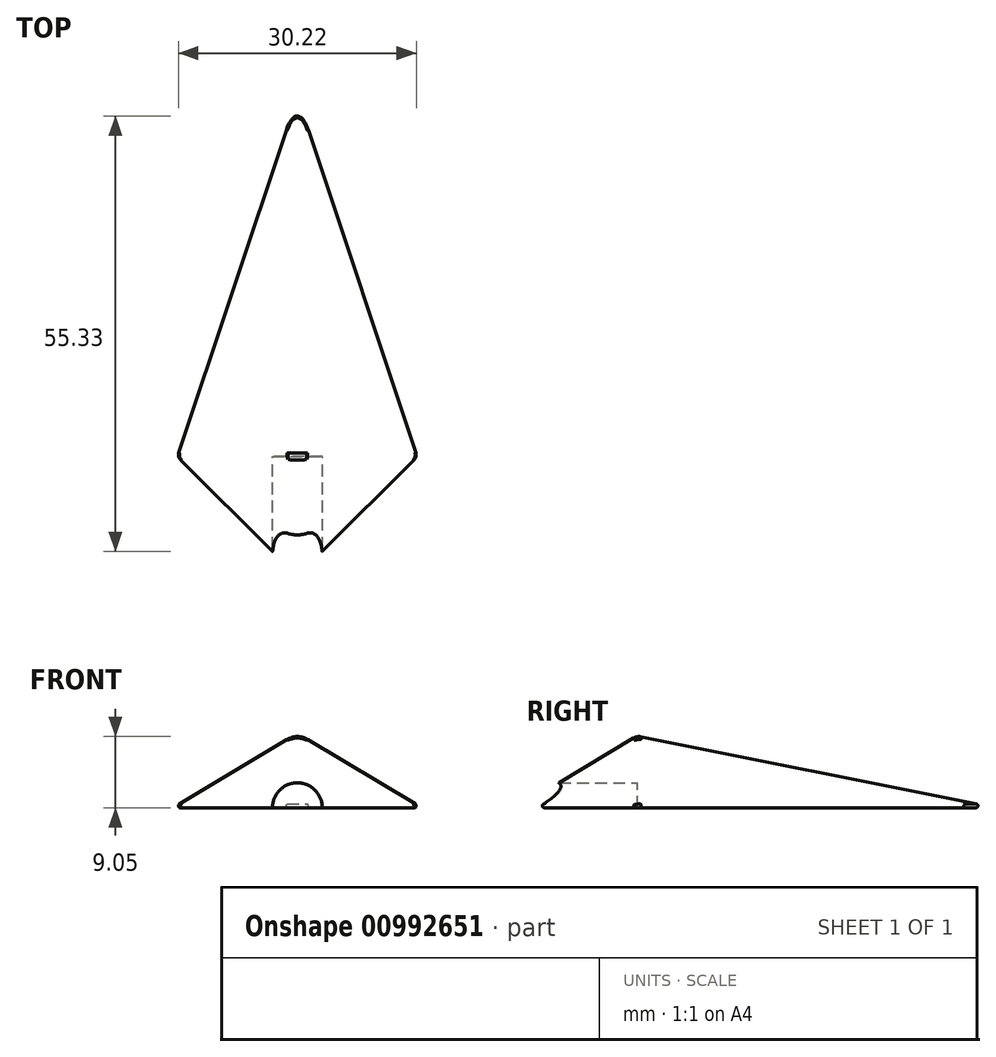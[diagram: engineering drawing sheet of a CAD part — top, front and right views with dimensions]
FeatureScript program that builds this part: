
annotation { "Feature Type Name" : "Feature", "Feature Type Description" : "" }
export const myFeature = defineFeature(function(context is Context, id is Id, definition is map)
    precondition{}
    {
        {
            var Q0;
            Q0=qCreatedBy(makeId("Top.planeOp"),FACE);
            var sketch = newSketch(context, id + "F0", { "sketchPlane" : qUnion([Q0])});
            skLineSegment(sketch, "E0", {"start": v(-15.88, 0) * mm, "end": v(15.88, 0) * mm});
            skLineSegment(sketch, "E1", {"start": v(0, -15.88) * mm, "end": v(0, 47.62) * mm});
            skLineSegment(sketch, "E2", {"start": v(-15.88, 0) * mm, "end": v(0, 47.62) * mm});
            skLineSegment(sketch, "E3", {"start": v(15.87, 0) * mm, "end": v(0, 47.63) * mm});
            skLineSegment(sketch, "E4", {"start": v(-15.88, 0) * mm, "end": v(0, -15.88) * mm});
            skLineSegment(sketch, "E5", {"start": v(15.88, 0) * mm, "end": v(0, -15.88) * mm});
            skSolve(sketch);
        }
        {
            var Q0;
            Q0=qCreatedBy(makeId("Right.planeOp"),FACE);
            var sketch = newSketch(context, id + "F1", { "sketchPlane" : qUnion([Q0])});
            skLineSegment(sketch, "E6", {"start": v(-15.88, 0) * mm, "end": v(47.62, 0) * mm});
            skLineSegment(sketch, "E7", {"start": v(0, 0) * mm, "end": v(0, 9.53) * mm});
            skLineSegment(sketch, "E8", {"start": v(47.62, 0) * mm, "end": v(0, 9.53) * mm});
            skLineSegment(sketch, "E9", {"start": v(-15.88, 0) * mm, "end": v(0, 9.52) * mm});
            skSolve(sketch);
        }
        {
            var Q0;
            Q0=qCreatedBy(makeId("Front.planeOp"),FACE);
            var sketch = newSketch(context, id + "F2", { "sketchPlane" : qUnion([Q0])});
            skLineSegment(sketch, "E10", {"start": v(-15.88, 0) * mm, "end": v(0, 9.52) * mm});
            skLineSegment(sketch, "E11", {"start": v(0, 9.52) * mm, "end": v(15.88, 0) * mm});
            skLineSegment(sketch, "E12", {"start": v(15.88, 0) * mm, "end": v(-15.88, 0) * mm});
            skSolve(sketch);
        }
        {
            var Q0;
            {var subQ2=sQuery(id+"F1.wireOp",EDGE,"E7");Q0=makeQuery(id+"F1.imprint","IMPRINT",FACE,{"disambiguationData":[TD([[makeQuery(id+"F1.imprint","IMPRINT",EDGE,{"derivedFrom":subQ2}),-1.0]])]});}
            var Q1;
            {var subQ0=sQuery(id+"F0.wireOp",EDGE,"E2");Q1=makeQuery(id+"F0.imprint","IMPRINT",FACE,{"disambiguationData":[TD([[makeQuery(id+"F0.imprint","IMPRINT",EDGE,{"derivedFrom":subQ0}),-1.0]])]});}
            var Q2;
            Q2=sQuery(id+"F2.wireOp",EDGE,"E10");
            loft(context, id + "F3", {"addGuides" : true, "sheetProfilesArray" : [{ "sheetProfileEntities" : qUnion([Q0]) }, { "sheetProfileEntities" : qUnion([Q1]) }], "guidesArray" : [{ "guideEntities" : qUnion([Q2]), "guideDerivativeType" : LoftGuideDerivativeType.DEFAULT, "guideDerivativeMagnitude" : 1 }]});
        }
        {
            var Q1;
            {var subQ2=sQuery(id+"F1.wireOp",EDGE,"E7");Q1=makeQuery(id+"F1.imprint","IMPRINT",FACE,{"disambiguationData":[TD([[makeQuery(id+"F1.imprint","IMPRINT",EDGE,{"derivedFrom":subQ2}),1.0]])]});}
            var Q2;
            {var subQ0=sQuery(id+"F0.wireOp",EDGE,"E4");Q2=makeQuery(id+"F0.imprint","IMPRINT",FACE,{"disambiguationData":[TD([[makeQuery(id+"F0.imprint","IMPRINT",EDGE,{"derivedFrom":subQ0}),1.0]])]});}
            var Q3;
            Q3=sQuery(id+"F2.wireOp",EDGE,"E10");
            loft(context, id + "F4", {"operationType" : NewBodyOperationType.ADD, "addGuides" : true, "sheetProfilesArray" : [{ "sheetProfileEntities" : qUnion([Q1]) }, { "sheetProfileEntities" : qUnion([Q2]) }], "guidesArray" : [{ "guideEntities" : qUnion([Q3]), "guideDerivativeType" : LoftGuideDerivativeType.DEFAULT, "guideDerivativeMagnitude" : 1 }]});
        }
        {
            var Q1;
            {var subQ2=sQuery(id+"F1.wireOp",EDGE,"E7");Q1=makeQuery(id+"F1.imprint","IMPRINT",FACE,{"disambiguationData":[TD([[makeQuery(id+"F1.imprint","IMPRINT",EDGE,{"derivedFrom":subQ2}),1.0]])]});}
            var Q2;
            {var subQ0=sQuery(id+"F0.wireOp",EDGE,"E5");Q2=makeQuery(id+"F0.imprint","IMPRINT",FACE,{"disambiguationData":[TD([[makeQuery(id+"F0.imprint","IMPRINT",EDGE,{"derivedFrom":subQ0}),-1.0]])]});}
            var Q3;
            Q3=sQuery(id+"F2.wireOp",EDGE,"E11");
            loft(context, id + "F5", {"operationType" : NewBodyOperationType.ADD, "addGuides" : true, "sheetProfilesArray" : [{ "sheetProfileEntities" : qUnion([Q1]) }, { "sheetProfileEntities" : qUnion([Q2]) }], "guidesArray" : [{ "guideEntities" : qUnion([Q3]), "guideDerivativeType" : LoftGuideDerivativeType.DEFAULT, "guideDerivativeMagnitude" : 1 }]});
        }
        {
            var Q1;
            {var subQ2=sQuery(id+"F1.wireOp",EDGE,"E7");Q1=makeQuery(id+"F1.imprint","IMPRINT",FACE,{"disambiguationData":[TD([[makeQuery(id+"F1.imprint","IMPRINT",EDGE,{"derivedFrom":subQ2}),-1.0]])]});}
            var Q2;
            {var subQ0=sQuery(id+"F0.wireOp",EDGE,"E3");Q2=makeQuery(id+"F0.imprint","IMPRINT",FACE,{"disambiguationData":[TD([[makeQuery(id+"F0.imprint","IMPRINT",EDGE,{"derivedFrom":subQ0}),1.0]])]});}
            var Q3;
            Q3=sQuery(id+"F2.wireOp",EDGE,"E11");
            loft(context, id + "F6", {"operationType" : NewBodyOperationType.ADD, "addGuides" : true, "sheetProfilesArray" : [{ "sheetProfileEntities" : qUnion([Q1]) }, { "sheetProfileEntities" : qUnion([Q2]) }], "guidesArray" : [{ "guideEntities" : qUnion([Q3]), "guideDerivativeType" : LoftGuideDerivativeType.DEFAULT, "guideDerivativeMagnitude" : 1 }]});
        }
        {
            var Q0;
            Q0=qCreatedBy(makeId("Front.planeOp"),FACE);
            var sketch = newSketch(context, id + "F7", { "sketchPlane" : qUnion([Q0])});
            skCircle(sketch, "E13", {"center": v(0, 0) * mm, "radius": 3.18 * mm});
            skSolve(sketch);
        }
        {
            var Q0;
            Q0=makeQuery(id+"F7.imprint","IMPRINT",FACE,{"disambiguationData":[TD([[makeQuery(id+"F7.imprint","IMPRINT",EDGE,{"derivedFrom":sQuery(id+"F7.wireOp",EDGE,"E13")}),1.0]])]});
            var Q1;
            Q1=sQuery(id+"F7.wireOp",EDGE,"E13");
            extrude(context, id + "F8", {"entities" : qUnion([Q0]), "operationType" : NewBodyOperationType.REMOVE, "surfaceEntities" : qUnion([Q1]), "depth" : 25.4 * mm, "offsetDistance" : 25.4 * mm});
        }
        {
            var Q0;
            {var subQ0=sQuery(id+"F1.wireOp",EDGE,"E8");var subQ1=makeQuery(id+"F1.imprint","IMPRINT",EDGE,{"derivedFrom":subQ0});var subQ2=sQuery(id+"F1.wireOp",EDGE,"E9");var subQ3=sQuery(id+"F1.wireOp",EDGE,"E7");var subQ4=makeQuery(id+"F1.imprint","INTERSECT",VERTEX,{"derivedFrom":[subQ3,subQ0,subQ2]});var subQ5=sQuery(id+"F1.wireOp",EDGE,"E6");var subQ6=makeQuery(id+"F1.imprint","INTERSECT",VERTEX,{"derivedFrom":[subQ5,subQ0]});Q0=makeQuery(id+"F6.boolean.opBoolean","MERGE",EDGE,{"derivedFrom":[makeQuery(id+"F3.opLoft","MID_CAP_EDGE",EDGE,{"disambiguationData":[OSD([subQ5,subQ3,subQ0,subQ2]),TDD([subQ6,subQ4,subQ1])],"capPos":0.0}),makeQuery(id+"F6.opLoft","MID_CAP_EDGE",EDGE,{"disambiguationData":[OSD([subQ5,subQ3,subQ0,subQ2]),TDD([subQ6,subQ4,subQ1])],"capPos":0.0})]});}
            fillet(context, id + "F9", {"entities" : qUnion([Q0]), "radius" : 2.54 * mm, "tangentPropagation" : true, "allowEdgeOverflow" : false});
        }
        {
            var Q0;
            {var subQ0=sQuery(id+"F1.wireOp",EDGE,"E9");var subQ1=makeQuery(id+"F1.imprint","IMPRINT",EDGE,{"derivedFrom":subQ0});var subQ2=sQuery(id+"F1.wireOp",EDGE,"E8");var subQ3=sQuery(id+"F1.wireOp",EDGE,"E7");var subQ4=makeQuery(id+"F1.imprint","INTERSECT",VERTEX,{"derivedFrom":[subQ3,subQ2,subQ0]});var subQ5=sQuery(id+"F1.wireOp",EDGE,"E6");var subQ6=makeQuery(id+"F1.imprint","INTERSECT",VERTEX,{"derivedFrom":[subQ5,subQ0]});Q0=makeQuery(id+"F5.boolean.opBoolean","MERGE",EDGE,{"derivedFrom":[makeQuery(id+"F4.opLoft","MID_CAP_EDGE",EDGE,{"disambiguationData":[OSD([subQ5,subQ3,subQ2,subQ0]),TDD([subQ6,subQ4,subQ1])],"capPos":0.0}),makeQuery(id+"F5.opLoft","MID_CAP_EDGE",EDGE,{"disambiguationData":[OSD([subQ5,subQ3,subQ2,subQ0]),TDD([subQ6,subQ4,subQ1])],"capPos":0.0})]});}
            fillet(context, id + "F10", {"entities" : qUnion([Q0]), "radius" : 2.54 * mm, "tangentPropagation" : true, "allowEdgeOverflow" : false});
        }
        {
            var Q0;
            Q0=makeQuery(id+"F3.opLoft","MID_CAP_EDGE",EDGE,{"disambiguationData":[OSD([sQuery(id+"F0.wireOp",EDGE,"E0"),sQuery(id+"F0.wireOp",EDGE,"E1"),sQuery(id+"F0.wireOp",EDGE,"E2"),sQuery(id+"F0.wireOp",EDGE,"E3"),sQuery(id+"F0.wireOp",EDGE,"E4")])],"capPos":1.0});
            var Q1;
            Q1=makeQuery(id+"F4.opLoft","MID_CAP_EDGE",EDGE,{"disambiguationData":[OSD([sQuery(id+"F0.wireOp",EDGE,"E0"),sQuery(id+"F0.wireOp",EDGE,"E1"),sQuery(id+"F0.wireOp",EDGE,"E2"),sQuery(id+"F0.wireOp",EDGE,"E4"),sQuery(id+"F0.wireOp",EDGE,"E5")])],"capPos":1.0});
            var Q2;
            Q2=makeQuery(id+"F5.opLoft","MID_CAP_EDGE",EDGE,{"disambiguationData":[OSD([sQuery(id+"F0.wireOp",EDGE,"E0"),sQuery(id+"F0.wireOp",EDGE,"E1"),sQuery(id+"F0.wireOp",EDGE,"E3"),sQuery(id+"F0.wireOp",EDGE,"E4"),sQuery(id+"F0.wireOp",EDGE,"E5")])],"capPos":1.0});
            fillet(context, id + "F11", {"entities" : qUnion([Q0, Q1, Q2]), "radius" : 0.25 * mm, "tangentPropagation" : true, "allowEdgeOverflow" : false});
        }
        {
            var Q0;
            {var subQ0=sQuery(id+"F2.wireOp",EDGE,"E10");var subQ1=sQuery(id+"F1.wireOp",EDGE,"E9");var subQ2=sQuery(id+"F1.wireOp",EDGE,"E8");var subQ3=sQuery(id+"F1.wireOp",EDGE,"E7");var subQ4=sQuery(id+"F0.wireOp",EDGE,"E4");var subQ5=sQuery(id+"F0.wireOp",EDGE,"E2");var subQ6=sQuery(id+"F0.wireOp",EDGE,"E0");Q0=makeQuery(id+"F4.boolean.opBoolean","MERGE",EDGE,{"derivedFrom":[makeQuery(id+"F3.opLoft","SWEPT_EDGE",EDGE,{"disambiguationData":[OSD([subQ6,subQ5,subQ4,subQ3,subQ2,subQ1,subQ0])]}),makeQuery(id+"F4.opLoft","SWEPT_EDGE",EDGE,{"disambiguationData":[OSD([subQ6,subQ5,subQ4,subQ3,subQ2,subQ1,subQ0])]})]});}
            fillet(context, id + "F12", {"entities" : qUnion([Q0]), "radius" : 1.27 * mm, "tangentPropagation" : true, "allowEdgeOverflow" : false});
        }
    });
